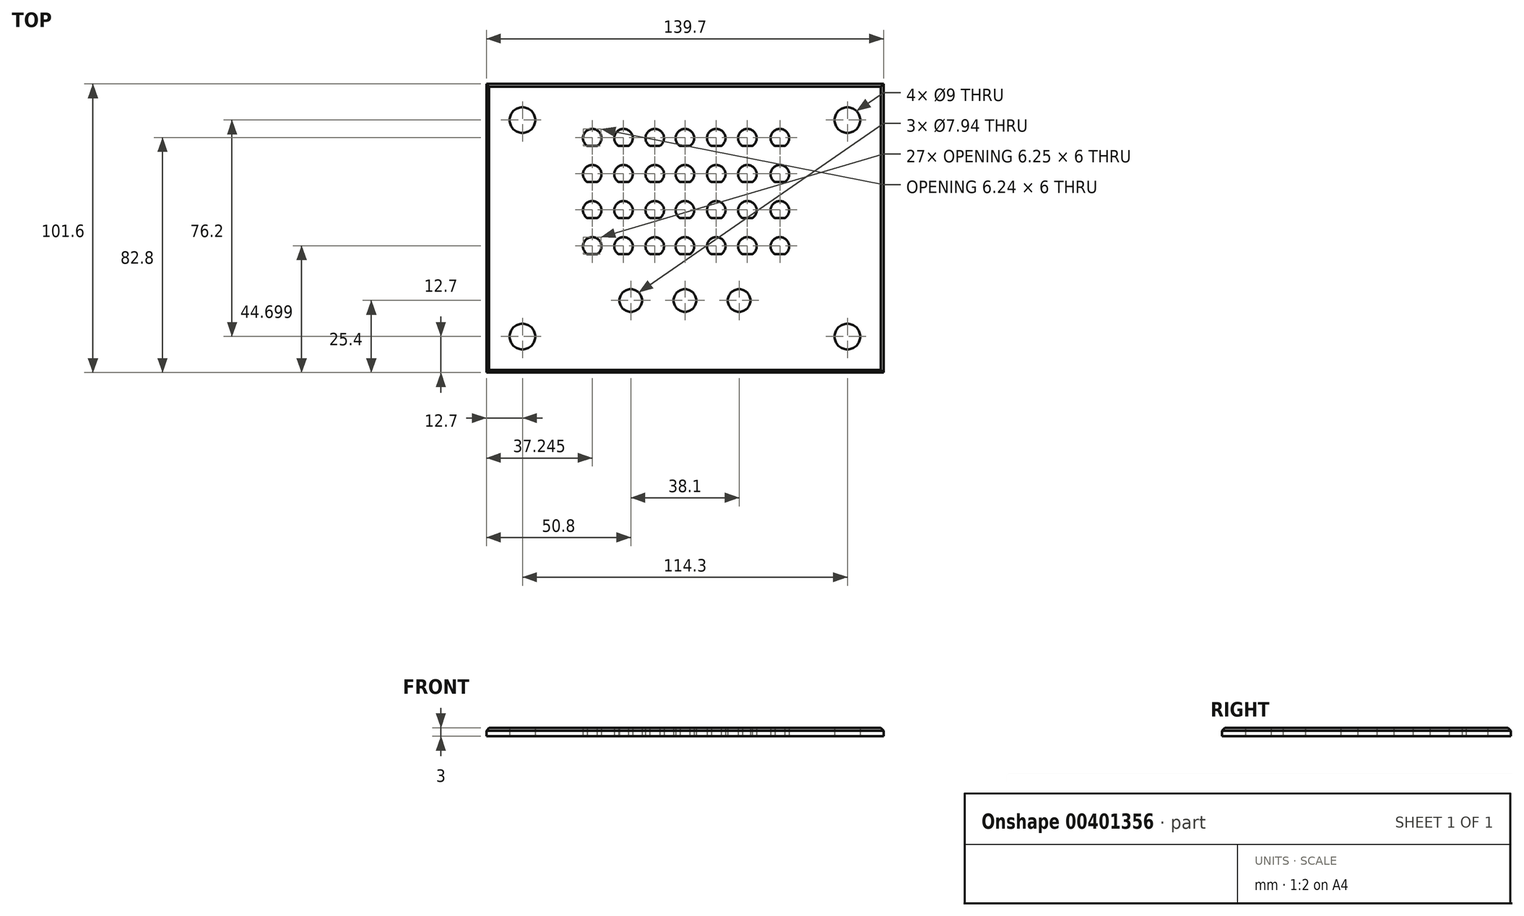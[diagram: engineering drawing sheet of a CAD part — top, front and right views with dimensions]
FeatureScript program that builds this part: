
annotation { "Feature Type Name" : "Feature", "Feature Type Description" : "" }
export const myFeature = defineFeature(function(context is Context, id is Id, definition is map)
    precondition{}
    {
        {
            var Q0;
            Q0=qCreatedBy(makeId("Top.planeOp"),FACE);
            var sketch = newSketch(context, id + "F0", { "sketchPlane" : qUnion([Q0])});
            skLineSegment(sketch, "E0.bottom", {"start": v(69.85, -50.8) * mm, "end": v(-69.85, -50.8) * mm});
            skLineSegment(sketch, "E0.top", {"start": v(69.85, 50.8) * mm, "end": v(-69.85, 50.8) * mm});
            skLineSegment(sketch, "E0.left", {"start": v(69.85, -50.8) * mm, "end": v(69.85, 50.8) * mm});
            skLineSegment(sketch, "E0.right", {"start": v(-69.85, -50.8) * mm, "end": v(-69.85, 50.8) * mm});
            skPoint(sketch, "E0.middle", {"position": v(0, 0) * mm});
            skLineSegment(sketch, "E1", {"start": v(-37.18, 31.75) * mm, "end": v(37.18, 31.75) * mm, "construction": true});
            skLineSegment(sketch, "E2", {"start": v(-37.24, 19.05) * mm, "end": v(37.24, 19.05) * mm, "construction": true});
            skLineSegment(sketch, "E3", {"start": v(-37.46, 6.35) * mm, "end": v(37.24, 6.35) * mm, "construction": true});
            skLineSegment(sketch, "E4", {"start": v(-37.55, -6.35) * mm, "end": v(37.34, -6.35) * mm, "construction": true});
            skLineSegment(sketch, "E5", {"start": v(0, -7.88) * mm, "end": v(0, 50.8) * mm, "construction": true});
            skLineSegment(sketch, "E6", {"start": v(-10.6, -8.64) * mm, "end": v(-10.6, 50.8) * mm, "construction": true});
            skLineSegment(sketch, "E7", {"start": v(-21.6, -7.88) * mm, "end": v(-21.6, 50.8) * mm, "construction": true});
            skLineSegment(sketch, "E8", {"start": v(-32.6, -8.4) * mm, "end": v(-32.6, 50.8) * mm, "construction": true});
            skLineSegment(sketch, "E9", {"start": v(11, -8.95) * mm, "end": v(11, 50.8) * mm, "construction": true});
            skLineSegment(sketch, "E10", {"start": v(21.96, -8.95) * mm, "end": v(21.96, 50.8) * mm, "construction": true});
            skLineSegment(sketch, "E11", {"start": v(33.4, -9.19) * mm, "end": v(33.4, 50.8) * mm, "construction": true});
            skCircle(sketch, "E12", {"center": v(-32.6, 31.75) * mm, "radius": 3.25 * mm});
            skCircle(sketch, "E13", {"center": v(-21.6, 31.75) * mm, "radius": 3.25 * mm});
            skCircle(sketch, "E14", {"center": v(-10.6, 31.75) * mm, "radius": 3.25 * mm});
            skCircle(sketch, "E15", {"center": v(0, 31.75) * mm, "radius": 3.25 * mm});
            skCircle(sketch, "E16", {"center": v(11, 31.75) * mm, "radius": 3.25 * mm});
            skCircle(sketch, "E17", {"center": v(21.96, 31.75) * mm, "radius": 3.25 * mm});
            skCircle(sketch, "E18", {"center": v(33.4, 31.75) * mm, "radius": 3.25 * mm});
            skLineSegment(sketch, "E19", {"start": v(-36.74, -25.4) * mm, "end": v(36.74, -25.4) * mm, "construction": true});
            skPoint(sketch, "E20", {"position": v(0, -25.4) * mm});
            skCircle(sketch, "E21", {"center": v(0, -25.4) * mm, "radius": 3.97 * mm});
            skCircle(sketch, "E22", {"center": v(19.05, -25.4) * mm, "radius": 3.97 * mm});
            skCircle(sketch, "E23", {"center": v(-19.05, -25.4) * mm, "radius": 3.97 * mm});
            skLineSegment(sketch, "E24.bottom", {"start": v(38.1, -38.1) * mm, "end": v(-38.1, -38.1) * mm, "construction": true});
            skLineSegment(sketch, "E24.top", {"start": v(38.1, 38.1) * mm, "end": v(-38.1, 38.1) * mm, "construction": true});
            skLineSegment(sketch, "E24.left", {"start": v(38.1, -38.1) * mm, "end": v(38.1, 38.1) * mm, "construction": true});
            skLineSegment(sketch, "E24.right", {"start": v(-38.1, -38.1) * mm, "end": v(-38.1, 38.1) * mm, "construction": true});
            skCircle(sketch, "E25", {"center": v(-57.15, -38.1) * mm, "radius": 4.5 * mm});
            skLineSegment(sketch, "E26", {"start": v(-57.15, -47.32) * mm, "end": v(-57.15, 45.96) * mm, "construction": true});
            skLineSegment(sketch, "E27", {"start": v(-65.5, -38.1) * mm, "end": v(68.65, -38.1) * mm, "construction": true});
            skLineSegment(sketch, "E28", {"start": v(57.15, -46.6) * mm, "end": v(57.15, 47.13) * mm, "construction": true});
            skLineSegment(sketch, "E29", {"start": v(-64.4, 44.45) * mm, "end": v(66.43, 44.45) * mm, "construction": true});
            skCircle(sketch, "E30", {"center": v(57.15, -38.1) * mm, "radius": 4.5 * mm});
            skCircle(sketch, "E31", {"center": v(57.15, 38.1) * mm, "radius": 4.5 * mm});
            skCircle(sketch, "E32", {"center": v(-57.15, 38.1) * mm, "radius": 4.5 * mm});
            skLineSegment(sketch, "E33", {"start": v(-23.34, 29) * mm, "end": v(-19.88, 29) * mm});
            skLineSegment(sketch, "E34", {"start": v(-34.34, 29) * mm, "end": v(-30.87, 29) * mm});
            skLineSegment(sketch, "E35", {"start": v(-12.33, 29) * mm, "end": v(-8.88, 29) * mm});
            skLineSegment(sketch, "E36", {"start": v(-1.73, 29) * mm, "end": v(1.73, 29) * mm});
            skLineSegment(sketch, "E37", {"start": v(9.27, 29) * mm, "end": v(12.73, 29) * mm});
            skLineSegment(sketch, "E38", {"start": v(-32.6, 35) * mm, "end": v(-29.97, 35) * mm});
            skCircle(sketch, "E39", {"center": v(-32.6, 19.05) * mm, "radius": 3.25 * mm});
            skCircle(sketch, "E40", {"center": v(-21.6, 19.05) * mm, "radius": 3.25 * mm});
            skCircle(sketch, "E41", {"center": v(-10.6, 19.05) * mm, "radius": 3.25 * mm});
            skLineSegment(sketch, "E42", {"start": v(-23.34, 16.3) * mm, "end": v(-19.88, 16.3) * mm});
            skLineSegment(sketch, "E43", {"start": v(-12.34, 16.3) * mm, "end": v(-8.88, 16.3) * mm});
            skLineSegment(sketch, "E44", {"start": v(-34.34, 16.3) * mm, "end": v(-30.88, 16.3) * mm});
            skCircle(sketch, "E45", {"center": v(0, 19.05) * mm, "radius": 3.25 * mm});
            skCircle(sketch, "E46", {"center": v(11, 19.05) * mm, "radius": 3.25 * mm});
            skCircle(sketch, "E47", {"center": v(21.96, 19.05) * mm, "radius": 3.25 * mm});
            skCircle(sketch, "E48", {"center": v(33.4, 19.05) * mm, "radius": 3.25 * mm});
            skLineSegment(sketch, "E49", {"start": v(31.66, 16.3) * mm, "end": v(35.12, 16.3) * mm});
            skLineSegment(sketch, "E50", {"start": v(-1.73, 16.3) * mm, "end": v(1.73, 16.3) * mm});
            skLineSegment(sketch, "E51", {"start": v(9.27, 16.3) * mm, "end": v(12.73, 16.3) * mm});
            skCircle(sketch, "E52", {"center": v(-32.6, 6.35) * mm, "radius": 3.25 * mm});
            skCircle(sketch, "E53", {"center": v(-21.6, 6.35) * mm, "radius": 3.25 * mm});
            skCircle(sketch, "E54", {"center": v(-10.6, 6.35) * mm, "radius": 3.25 * mm});
            skCircle(sketch, "E55", {"center": v(0, 6.35) * mm, "radius": 3.25 * mm});
            skCircle(sketch, "E56", {"center": v(11, 6.35) * mm, "radius": 3.25 * mm});
            skCircle(sketch, "E57", {"center": v(21.96, 6.35) * mm, "radius": 3.25 * mm});
            skCircle(sketch, "E58", {"center": v(33.4, 6.35) * mm, "radius": 3.25 * mm});
            skLineSegment(sketch, "E59", {"start": v(-23.34, 3.6) * mm, "end": v(-19.88, 3.6) * mm});
            skLineSegment(sketch, "E60", {"start": v(-34.34, 3.6) * mm, "end": v(-30.88, 3.6) * mm});
            skLineSegment(sketch, "E61", {"start": v(-12.34, 3.6) * mm, "end": v(-8.88, 3.6) * mm});
            skLineSegment(sketch, "E62", {"start": v(-1.73, 3.6) * mm, "end": v(1.73, 3.6) * mm});
            skLineSegment(sketch, "E63", {"start": v(9.27, 3.6) * mm, "end": v(12.73, 3.6) * mm});
            skCircle(sketch, "E64", {"center": v(-32.6, -6.35) * mm, "radius": 3.25 * mm});
            skCircle(sketch, "E65", {"center": v(-21.6, -6.35) * mm, "radius": 3.25 * mm});
            skCircle(sketch, "E66", {"center": v(-10.6, -6.35) * mm, "radius": 3.25 * mm});
            skLineSegment(sketch, "E67", {"start": v(-23.34, -9.1) * mm, "end": v(-19.88, -9.1) * mm});
            skLineSegment(sketch, "E68", {"start": v(-12.34, -9.1) * mm, "end": v(-8.88, -9.1) * mm});
            skLineSegment(sketch, "E69", {"start": v(-34.34, -9.1) * mm, "end": v(-30.88, -9.1) * mm});
            skCircle(sketch, "E70", {"center": v(11, -6.35) * mm, "radius": 3.25 * mm});
            skCircle(sketch, "E71", {"center": v(21.96, -6.35) * mm, "radius": 3.25 * mm});
            skCircle(sketch, "E72", {"center": v(33.4, -6.35) * mm, "radius": 3.25 * mm});
            skLineSegment(sketch, "E73", {"start": v(20.23, -9.1) * mm, "end": v(23.7, -9.1) * mm});
            skLineSegment(sketch, "E74", {"start": v(31.66, -9.1) * mm, "end": v(34.6, -9.1) * mm});
            skLineSegment(sketch, "E75", {"start": v(9.27, -9.1) * mm, "end": v(12.73, -9.1) * mm});
            skCircle(sketch, "E76", {"center": v(0, -6.35) * mm, "radius": 3.25 * mm});
            skLineSegment(sketch, "E77", {"start": v(-1.73, -9.1) * mm, "end": v(1.73, -9.1) * mm});
            skLineSegment(sketch, "E78", {"start": v(20.23, 29) * mm, "end": v(23.7, 29) * mm});
            skLineSegment(sketch, "E79", {"start": v(20.23, 16.3) * mm, "end": v(23.7, 16.3) * mm});
            skLineSegment(sketch, "E80", {"start": v(35.12, 16.3) * mm, "end": v(35.12, 16.3) * mm});
            skLineSegment(sketch, "E81", {"start": v(20.23, 3.6) * mm, "end": v(23.7, 3.6) * mm});
            skLineSegment(sketch, "E82", {"start": v(34.6, -9.1) * mm, "end": v(35.12, -9.1) * mm});
            skLineSegment(sketch, "E83", {"start": v(23.7, -9.1) * mm, "end": v(23.7, -9.1) * mm});
            skLineSegment(sketch, "E84", {"start": v(31.66, 29) * mm, "end": v(35.12, 29) * mm});
            skLineSegment(sketch, "E85", {"start": v(31.66, 3.6) * mm, "end": v(35.12, 3.6) * mm});
            skSolve(sketch);
        }
        {
            var Q0;
            Q0=makeQuery(id+"F0.imprint","IMPRINT",FACE,{"disambiguationData":[TD([[makeQuery(id+"F0.imprint","IMPRINT",EDGE,{"derivedFrom":sQuery(id+"F0.wireOp",EDGE,"E0.bottom")}),-1.0]])]});
            var Q1;
            {var subQ0=sQuery(id+"F0.wireOp",EDGE,"E44");Q1=makeQuery(id+"F0.imprint","IMPRINT",FACE,{"disambiguationData":[TD([[makeQuery(id+"F0.imprint","IMPRINT",EDGE,{"derivedFrom":subQ0}),-1.0]])]});}
            var Q2;
            {var subQ0=sQuery(id+"F0.wireOp",EDGE,"E42");Q2=makeQuery(id+"F0.imprint","IMPRINT",FACE,{"disambiguationData":[TD([[makeQuery(id+"F0.imprint","IMPRINT",EDGE,{"derivedFrom":subQ0}),-1.0]])]});}
            var Q3;
            {var subQ0=sQuery(id+"F0.wireOp",EDGE,"E43");Q3=makeQuery(id+"F0.imprint","IMPRINT",FACE,{"disambiguationData":[TD([[makeQuery(id+"F0.imprint","IMPRINT",EDGE,{"derivedFrom":subQ0}),-1.0]])]});}
            var Q4;
            {var subQ0=sQuery(id+"F0.wireOp",EDGE,"E60");Q4=makeQuery(id+"F0.imprint","IMPRINT",FACE,{"disambiguationData":[TD([[makeQuery(id+"F0.imprint","IMPRINT",EDGE,{"derivedFrom":subQ0}),-1.0]])]});}
            var Q5;
            {var subQ0=sQuery(id+"F0.wireOp",EDGE,"E59");Q5=makeQuery(id+"F0.imprint","IMPRINT",FACE,{"disambiguationData":[TD([[makeQuery(id+"F0.imprint","IMPRINT",EDGE,{"derivedFrom":subQ0}),-1.0]])]});}
            var Q6;
            {var subQ0=sQuery(id+"F0.wireOp",EDGE,"E61");Q6=makeQuery(id+"F0.imprint","IMPRINT",FACE,{"disambiguationData":[TD([[makeQuery(id+"F0.imprint","IMPRINT",EDGE,{"derivedFrom":subQ0}),-1.0]])]});}
            var Q7;
            {var subQ0=sQuery(id+"F0.wireOp",EDGE,"E50");Q7=makeQuery(id+"F0.imprint","IMPRINT",FACE,{"disambiguationData":[TD([[makeQuery(id+"F0.imprint","IMPRINT",EDGE,{"derivedFrom":subQ0}),-1.0]])]});}
            var Q8;
            {var subQ0=sQuery(id+"F0.wireOp",EDGE,"E62");Q8=makeQuery(id+"F0.imprint","IMPRINT",FACE,{"disambiguationData":[TD([[makeQuery(id+"F0.imprint","IMPRINT",EDGE,{"derivedFrom":subQ0}),-1.0]])]});}
            var Q9;
            {var subQ0=sQuery(id+"F0.wireOp",EDGE,"E63");Q9=makeQuery(id+"F0.imprint","IMPRINT",FACE,{"disambiguationData":[TD([[makeQuery(id+"F0.imprint","IMPRINT",EDGE,{"derivedFrom":subQ0}),-1.0]])]});}
            var Q10;
            {var subQ0=sQuery(id+"F0.wireOp",EDGE,"E51");Q10=makeQuery(id+"F0.imprint","IMPRINT",FACE,{"disambiguationData":[TD([[makeQuery(id+"F0.imprint","IMPRINT",EDGE,{"derivedFrom":subQ0}),-1.0]])]});}
            var Q11;
            {var subQ0=sQuery(id+"F0.wireOp",EDGE,"E79");Q11=makeQuery(id+"F0.imprint","IMPRINT",FACE,{"disambiguationData":[TD([[makeQuery(id+"F0.imprint","IMPRINT",EDGE,{"derivedFrom":subQ0}),-1.0]])]});}
            var Q12;
            {var subQ0=sQuery(id+"F0.wireOp",EDGE,"E81");Q12=makeQuery(id+"F0.imprint","IMPRINT",FACE,{"disambiguationData":[TD([[makeQuery(id+"F0.imprint","IMPRINT",EDGE,{"derivedFrom":subQ0}),-1.0]])]});}
            var Q13;
            {var subQ0=sQuery(id+"F0.wireOp",EDGE,"E49");Q13=makeQuery(id+"F0.imprint","IMPRINT",FACE,{"disambiguationData":[TD([[makeQuery(id+"F0.imprint","IMPRINT",EDGE,{"derivedFrom":subQ0}),-1.0]])]});}
            var Q14;
            {var subQ0=sQuery(id+"F0.wireOp",EDGE,"E85");Q14=makeQuery(id+"F0.imprint","IMPRINT",FACE,{"disambiguationData":[TD([[makeQuery(id+"F0.imprint","IMPRINT",EDGE,{"derivedFrom":subQ0}),-1.0]])]});}
            var Q15;
            {var subQ0=sQuery(id+"F0.wireOp",EDGE,"E74");Q15=makeQuery(id+"F0.imprint","IMPRINT",FACE,{"disambiguationData":[TD([[makeQuery(id+"F0.imprint","IMPRINT",EDGE,{"derivedFrom":subQ0}),-1.0]])]});}
            var Q16;
            {var subQ0=sQuery(id+"F0.wireOp",EDGE,"E73");Q16=makeQuery(id+"F0.imprint","IMPRINT",FACE,{"disambiguationData":[TD([[makeQuery(id+"F0.imprint","IMPRINT",EDGE,{"derivedFrom":subQ0}),-1.0]])]});}
            var Q17;
            {var subQ0=sQuery(id+"F0.wireOp",EDGE,"E75");Q17=makeQuery(id+"F0.imprint","IMPRINT",FACE,{"disambiguationData":[TD([[makeQuery(id+"F0.imprint","IMPRINT",EDGE,{"derivedFrom":subQ0}),-1.0]])]});}
            var Q18;
            {var subQ0=sQuery(id+"F0.wireOp",EDGE,"E77");Q18=makeQuery(id+"F0.imprint","IMPRINT",FACE,{"disambiguationData":[TD([[makeQuery(id+"F0.imprint","IMPRINT",EDGE,{"derivedFrom":subQ0}),-1.0]])]});}
            var Q19;
            {var subQ0=sQuery(id+"F0.wireOp",EDGE,"E68");Q19=makeQuery(id+"F0.imprint","IMPRINT",FACE,{"disambiguationData":[TD([[makeQuery(id+"F0.imprint","IMPRINT",EDGE,{"derivedFrom":subQ0}),-1.0]])]});}
            var Q20;
            {var subQ0=sQuery(id+"F0.wireOp",EDGE,"E67");Q20=makeQuery(id+"F0.imprint","IMPRINT",FACE,{"disambiguationData":[TD([[makeQuery(id+"F0.imprint","IMPRINT",EDGE,{"derivedFrom":subQ0}),-1.0]])]});}
            var Q21;
            {var subQ0=sQuery(id+"F0.wireOp",EDGE,"E69");Q21=makeQuery(id+"F0.imprint","IMPRINT",FACE,{"disambiguationData":[TD([[makeQuery(id+"F0.imprint","IMPRINT",EDGE,{"derivedFrom":subQ0}),-1.0]])]});}
            var Q22;
            {var subQ0=sQuery(id+"F0.wireOp",EDGE,"E34");Q22=makeQuery(id+"F0.imprint","IMPRINT",FACE,{"disambiguationData":[TD([[makeQuery(id+"F0.imprint","IMPRINT",EDGE,{"derivedFrom":subQ0}),-1.0]])]});}
            var Q23;
            {var subQ0=sQuery(id+"F0.wireOp",EDGE,"E33");Q23=makeQuery(id+"F0.imprint","IMPRINT",FACE,{"disambiguationData":[TD([[makeQuery(id+"F0.imprint","IMPRINT",EDGE,{"derivedFrom":subQ0}),-1.0]])]});}
            var Q24;
            {var subQ0=sQuery(id+"F0.wireOp",EDGE,"E35");Q24=makeQuery(id+"F0.imprint","IMPRINT",FACE,{"disambiguationData":[TD([[makeQuery(id+"F0.imprint","IMPRINT",EDGE,{"derivedFrom":subQ0}),-1.0]])]});}
            var Q25;
            {var subQ0=sQuery(id+"F0.wireOp",EDGE,"E36");Q25=makeQuery(id+"F0.imprint","IMPRINT",FACE,{"disambiguationData":[TD([[makeQuery(id+"F0.imprint","IMPRINT",EDGE,{"derivedFrom":subQ0}),-1.0]])]});}
            var Q26;
            {var subQ0=sQuery(id+"F0.wireOp",EDGE,"E37");Q26=makeQuery(id+"F0.imprint","IMPRINT",FACE,{"disambiguationData":[TD([[makeQuery(id+"F0.imprint","IMPRINT",EDGE,{"derivedFrom":subQ0}),-1.0]])]});}
            var Q27;
            {var subQ0=sQuery(id+"F0.wireOp",EDGE,"E78");Q27=makeQuery(id+"F0.imprint","IMPRINT",FACE,{"disambiguationData":[TD([[makeQuery(id+"F0.imprint","IMPRINT",EDGE,{"derivedFrom":subQ0}),-1.0]])]});}
            var Q28;
            {var subQ0=sQuery(id+"F0.wireOp",EDGE,"E84");Q28=makeQuery(id+"F0.imprint","IMPRINT",FACE,{"disambiguationData":[TD([[makeQuery(id+"F0.imprint","IMPRINT",EDGE,{"derivedFrom":subQ0}),-1.0]])]});}
            extrude(context, id + "F1", {"entities" : qUnion([Q0, Q1, Q2, Q3, Q4, Q5, Q6, Q7, Q8, Q9, Q10, Q11, Q12, Q13, Q14, Q15, Q16, Q17, Q18, Q19, Q20, Q21, Q22, Q23, Q24, Q25, Q26, Q27, Q28]), "depth" : 3 * mm, "offsetDistance" : 25 * mm});
        }
        {
            var Q0;
            Q0=makeQuery(id+"F1.opExtrude","CAP_EDGE",EDGE,{"disambiguationData":[OSD([sQuery(id+"F0.wireOp",EDGE,"E0.top")])],"isStart":false});
            var Q1;
            Q1=makeQuery(id+"F1.opExtrude","CAP_EDGE",EDGE,{"disambiguationData":[OSD([sQuery(id+"F0.wireOp",EDGE,"E0.right")])],"isStart":false});
            var Q2;
            Q2=makeQuery(id+"F1.opExtrude","CAP_EDGE",EDGE,{"disambiguationData":[OSD([sQuery(id+"F0.wireOp",EDGE,"E0.left")])],"isStart":false});
            var Q3;
            Q3=makeQuery(id+"F1.opExtrude","CAP_EDGE",EDGE,{"disambiguationData":[OSD([sQuery(id+"F0.wireOp",EDGE,"E0.bottom")])],"isStart":false});
            chamfer(context, id + "F2", {"entities" : qUnion([Q0, Q1, Q2, Q3]), "width" : 1 * mm, "tangentPropagation" : true});
        }
    });
